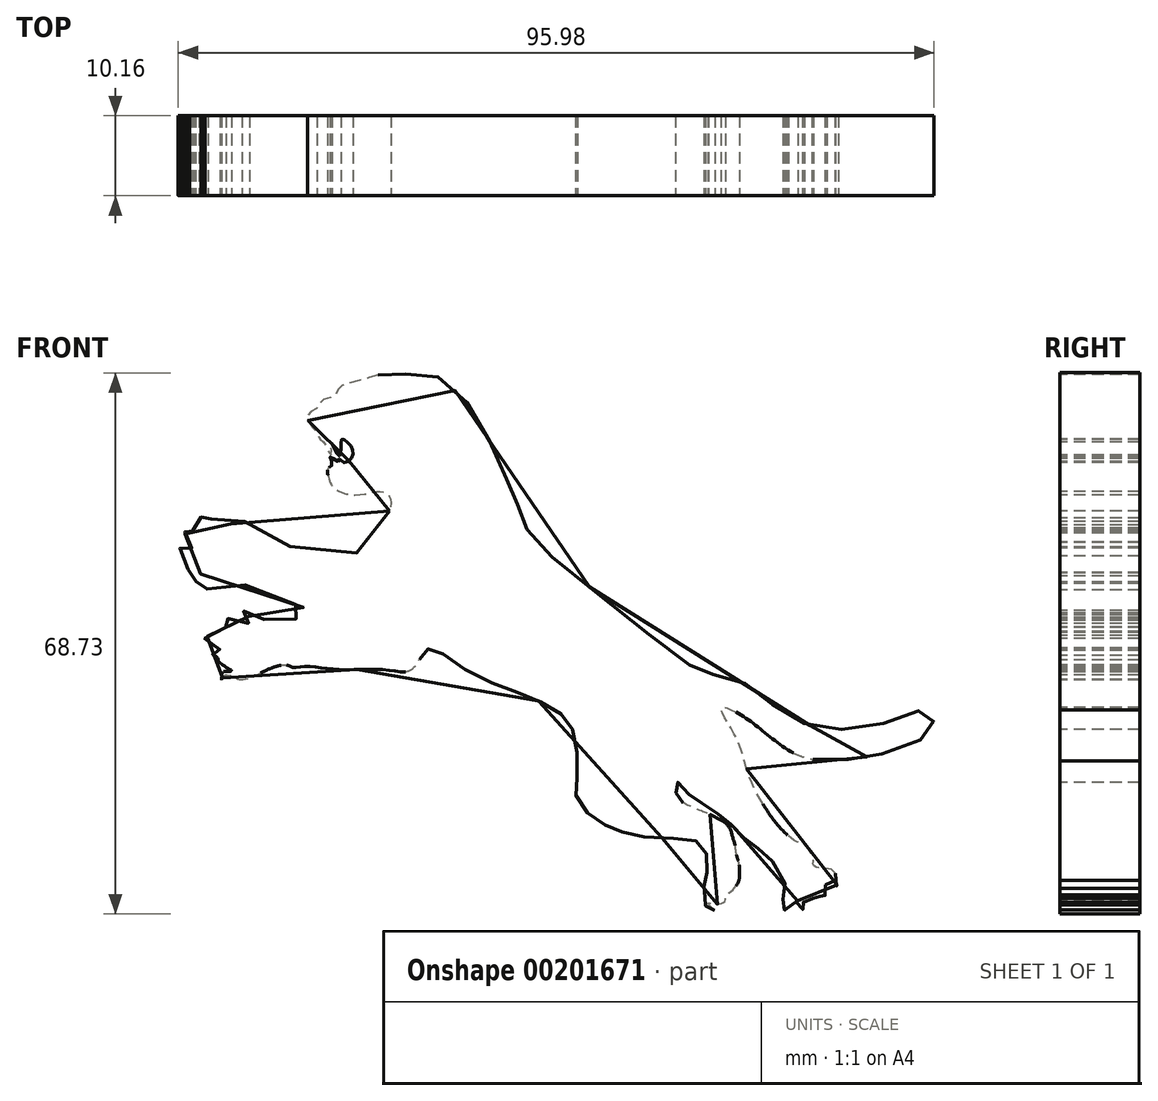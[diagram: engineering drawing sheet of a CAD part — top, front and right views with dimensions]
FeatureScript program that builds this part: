
annotation { "Feature Type Name" : "Feature", "Feature Type Description" : "" }
export const myFeature = defineFeature(function(context is Context, id is Id, definition is map)
    precondition{}
    {
        {
            var Q0;
            Q0=qCreatedBy(makeId("Front.planeOp"),FACE);
            var sketch = newSketch(context, id + "F0", { "sketchPlane" : qUnion([Q0])});
            skFitSpline(sketch, "E0", {"points": [v(-52.16, 5.65) * mm, v(-53.41, 3.78) * mm, v(-55.29, 0.96) * mm, v(-58.83, 0) * mm, v(-63.63, 0.86) * mm, v(-67.48, 2.1) * mm, v(-69.57, 3.67) * mm, v(-70.71, 4.3) * mm, v(-71.34, 3.57) * mm, v(-72.7, 4.2) * mm, v(-74.68, 4.61) * mm, v(-75.22, 4.82) * mm, v(-75.61, 4.82) * mm, v(-75.79, 5.22) * mm, v(-75.57, 5.68) * mm, v(-75.96, 5.52) * mm, v(-76.1, 4.9) * mm, v(-75.96, 4.12) * mm, v(-75.79, 3.83) * mm, v(-75.8, 3.2) * mm, v(-76.5, 3.37) * mm, v(-77.1, 3.22) * mm, v(-77.34, 2.9) * mm, v(-77.6, 3.05) * mm, v(-77.76, 3.55) * mm, v(-77.58, 3.9) * mm, v(-77.85, 3.73) * mm, v(-78.1, 3.29) * mm, v(-78.02, 2.39) * mm, v(-77.4, 1.69) * mm, v(-77.3, 1.75) * mm, v(-77.23, 1.34) * mm, v(-76.82, 0.99) * mm, v(-77.32, 0.96) * mm, v(-78.02, 0.42) * mm, v(-78.2, 0) * mm, v(-78.4, 0.2) * mm, v(-78.62, 0.4) * mm, v(-78.56, 1.08) * mm, v(-78.86, 0.8) * mm, v(-78.97, 0.12) * mm, v(-78.87, -0.52) * mm, v(-78.27, -0.9) * mm, v(-78.11, -1.37) * mm, v(-77.64, -1.81) * mm, v(-76.9, -2.15) * mm, v(-76.02, -2.16) * mm, v(-76.33, -2.51) * mm, v(-76.41, -3.3) * mm, v(-76.91, -3.11) * mm, v(-76.98, -2.59) * mm, v(-77.09, -3.01) * mm, v(-76.84, -3.84) * mm, v(-75.76, -4.18) * mm, v(-74.1, -4.32) * mm, v(-72.5, -3.79) * mm, v(-71.47, -3.55) * mm, v(-69.4, -4.12) * mm, v(-66.43, -5.19) * mm, v(-63.67, -6.36) * mm, v(-61.36, -7.6) * mm, v(-63.13, -7.8) * mm, v(-64.2, -8.12) * mm, v(-65.63, -8.93) * mm, v(-67.13, -8.9) * mm, v(-67.87, -8.32) * mm, v(-68.64, -7.82) * mm, v(-69.17, -7.82) * mm, v(-69.39, -7.24) * mm, v(-69.78, -7) * mm, v(-70.39, -6.96) * mm, v(-70.83, -7.2) * mm, v(-70.84, -7.55) * mm, v(-70.74, -7.36) * mm, v(-70.2, -7.3) * mm, v(-70.05, -7.9) * mm, v(-69.93, -8.34) * mm, v(-70.1, -8.58) * mm, v(-70.55, -8.25) * mm, v(-71.23, -8.08) * mm, v(-71.81, -8.08) * mm, v(-72.35, -8.18) * mm, v(-72.43, -8.22) * mm, v(-72.7, -7.94) * mm, v(-73.1, -7.82) * mm, v(-73.7, -8) * mm, v(-73.4, -8.06) * mm, v(-73.18, -8.1) * mm, v(-72.95, -8.65) * mm, v(-72.97, -9.12) * mm, v(-73.44, -9.12) * mm, v(-74.08, -9.76) * mm, v(-74.77, -9.6) * mm, v(-75.5, -10.08) * mm, v(-75.62, -10.54) * mm, v(-75.37, -10.29) * mm, v(-74.84, -10.15) * mm, v(-74.36, -10.68) * mm, v(-74.12, -11.3) * mm, v(-73.7, -11.77) * mm, v(-73.92, -12.04) * mm, v(-74.6, -12) * mm, v(-75.16, -12.87) * mm, v(-75.14, -13.24) * mm, v(-74.9, -12.87) * mm, v(-74.6, -12.64) * mm, v(-74.05, -12.9) * mm, v(-73.87, -13.36) * mm, v(-73.23, -13.97) * mm, v(-72.24, -14.62) * mm, v(-72.68, -14.69) * mm, v(-73.27, -14.74) * mm, v(-73.52, -15.36) * mm, v(-73.46, -15.77) * mm, v(-73.23, -15.28) * mm, v(-72.64, -15.18) * mm, v(-71.97, -15.33) * mm, v(-71.42, -15.66) * mm, v(-69.87, -15.5) * mm, v(-68.04, -14.65) * mm, v(-66.42, -14.02) * mm, v(-65.12, -13.92) * mm, v(-64.36, -14.21) * mm, v(-62.83, -14.06) * mm, v(-60.22, -14.32) * mm, v(-57.42, -14.48) * mm, v(-55.62, -14.44) * mm, v(-52.22, -14.54) * mm, v(-49.82, -14.67) * mm, v(-48.6, -13.62) * mm, v(-47.8, -12.32) * mm, v(-46.7, -11.73) * mm, v(-43.73, -13.7) * mm, v(-37.88, -16.65) * mm, v(-33.26, -18.41) * mm, v(-29.86, -20.56) * mm, v(-28.6, -23.2) * mm, v(-28.34, -28.08) * mm, v(-28.47, -30.5) * mm, v(-26.47, -33.17) * mm, v(-23.8, -34.64) * mm, v(-21.08, -35.53) * mm, v(-15.11, -35.98) * mm, v(-12.48, -36.65) * mm, v(-11.73, -39.18) * mm, v(-12.03, -41.15) * mm, v(-12.22, -42.4) * mm, v(-12.05, -43.3) * mm, v(-12.18, -43.88) * mm, v(-12.03, -44.46) * mm, v(-11.4, -44.86) * mm, v(-10.84, -45.02) * mm, v(-11.1, -44.8) * mm, v(-11.48, -44.46) * mm, v(-11.63, -44.1) * mm, v(-11.17, -44.22) * mm, v(-10, -44.18) * mm, v(-9.5, -43.78) * mm, v(-9.45, -43.17) * mm, v(-8.84, -42.72) * mm, v(-8.18, -42.02) * mm, v(-7.77, -41.19) * mm, v(-7.7, -40.27) * mm, v(-7.78, -39) * mm, v(-7.94, -38.5) * mm, v(-8.15, -37.52) * mm, v(-8.29, -36.67) * mm, v(-8.56, -35.78) * mm, v(-9, -34.52) * mm, v(-10.15, -33.47) * mm, v(-11.35, -32.9) * mm, v(-12.45, -32.46) * mm, v(-13.96, -31.83) * mm, v(-15.03, -31.28) * mm, v(-15.6, -30.67) * mm, v(-15.8, -29.96) * mm, v(-15.7, -29.12) * mm, v(-15.58, -28.78) * mm, v(-15.03, -29.4) * mm, v(-13.87, -30.53) * mm, v(-13, -31.18) * mm, v(-11.35, -32.08) * mm, v(-9.92, -33.26) * mm, v(-8.85, -34.06) * mm, v(-7.7, -35.36) * mm, v(-6.33, -36.41) * mm, v(-5.2, -37.3) * mm, v(-3.8, -38.46) * mm, v(-2, -41.28) * mm, v(-2.09, -42.88) * mm, v(-2.17, -43.8) * mm, v(-2, -44.11) * mm, v(-1.97, -45.04) * mm, v(-1.5, -45.49) * mm, v(-1.66, -45.1) * mm, v(-1.46, -44.34) * mm, v(-1.04, -44.3) * mm, v(-0.29, -43.83) * mm, v(-0.26, -44.23) * mm, v(0.53, -45.01) * mm, v(0.36, -44.5) * mm, v(0.39, -44.03) * mm, v(1.09, -44.17) * mm, v(1.62, -43.66) * mm, v(1.51, -43.1) * mm, v(2.24, -43.36) * mm, v(2.91, -43.22) * mm, v(3.22, -43.55) * mm, v(3.2, -42.94) * mm, v(3.42, -42.26) * mm, v(3.22, -41.84) * mm, v(3.87, -41.7) * mm, v(4.43, -41.22) * mm, v(4.46, -41.81) * mm, v(4.43, -42.23) * mm, v(4.76, -41.67) * mm, v(4.82, -40.78) * mm, v(4.23, -40.07) * mm, v(3.84, -39.82) * mm, v(1.8, -39.46) * mm, v(1.68, -38.62) * mm, v(1.15, -37.32) * mm, v(0.61, -36.8) * mm, v(-0.48, -36.31) * mm, v(-2.42, -34.69) * mm, v(-4.04, -32.61) * mm, v(-6.49, -28.04) * mm, v(-8.15, -23.05) * mm, v(-10, -19.35) * mm, v(-7.87, -20.02) * mm, v(-4.39, -22.55) * mm, v(-0.46, -25.24) * mm, v(3.86, -26.08) * mm, v(7.5, -25.69) * mm, v(11.43, -24.9) * mm, v(16.05, -22.9) * mm, v(17, -21.57) * mm, v(16.7, -20.49) * mm, v(15.77, -19.64) * mm, v(13.5, -20.3) * mm, v(7.93, -21.9) * mm, v(2.98, -21.9) * mm, v(-1.12, -20.58) * mm, v(-4.66, -17.94) * mm, v(-7.64, -15.9) * mm, v(-10.99, -15.1) * mm, v(-12.64, -14.68) * mm, v(-15.94, -12.56) * mm, v(-26.31, -4.34) * mm, v(-32.85, 1.07) * mm, v(-34.99, 3.87) * mm, v(-35.79, 5.94) * mm, v(-36.26, 8.07) * mm, v(-37.99, 10.8) * mm, v(-40.4, 16.75) * mm, v(-44.03, 21.2) * mm, v(-47.21, 23.17) * mm, v(-50.68, 23.03) * mm, v(-52.8, 23.1) * mm, v(-56.2, 22.18) * mm, v(-58.52, 21.33) * mm, v(-59.02, 20.42) * mm, v(-60.72, 19.7) * mm, v(-61.42, 18.72) * mm, v(-62.41, 18.08) * mm, v(-62.27, 16.67) * mm, v(-61.21, 15.4) * mm, v(-61.08, 14.8) * mm, v(-60.8, 14.82) * mm, v(-59.63, 12.81) * mm, v(-59.52, 13.28) * mm, v(-59.59, 14.42) * mm, v(-59.05, 13.4) * mm, v(-58.5, 12.66) * mm, v(-58.32, 13.64) * mm, v(-58.27, 14.75) * mm, v(-57.96, 14.77) * mm, v(-57.11, 14.02) * mm, v(-56.8, 13.15) * mm, v(-57.14, 12.17) * mm, v(-58.07, 11.88) * mm, v(-58.5, 12.32) * mm, v(-58.63, 11.99) * mm, v(-59.67, 12.6) * mm, v(-59.43, 11.59) * mm, v(-59.92, 11.14) * mm, v(-59.79, 9.52) * mm, v(-59.3, 8.7) * mm, v(-57.83, 7.9) * mm, v(-55.2, 7.85) * mm, v(-53.4, 8.18) * mm, v(-52.17, 7.51) * mm, v(-52.16, 5.65) * mm]});
            skSolve(sketch);
        }
        {
            var Q0;
            Q0 = qSketchRegion(id + "F0", true);
            extrude(context, id + "F1", {"entities" : qUnion([Q0]), "oppositeDirection" : true, "depth" : 10.16 * mm});
        }
    });
